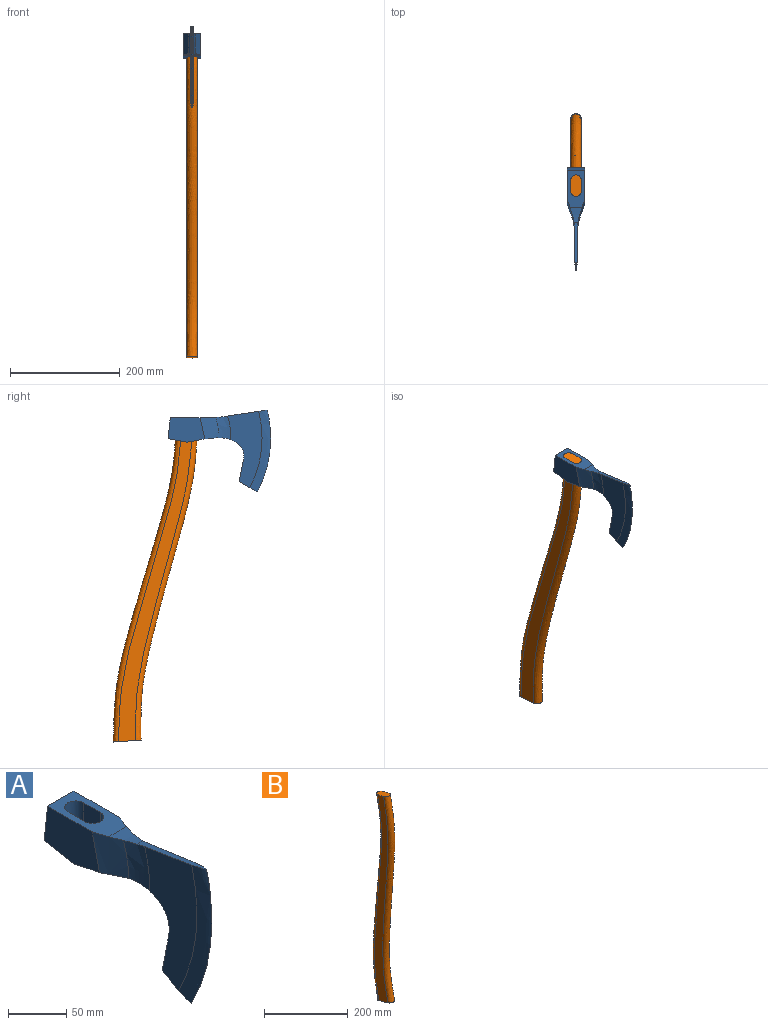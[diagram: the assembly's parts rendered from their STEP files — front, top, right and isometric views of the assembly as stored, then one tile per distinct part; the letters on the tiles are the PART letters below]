
ASSEMBLY  parts=2 mates=1
PART A: 27 faces, bbox 32.4x187.8x151 mm
  f0: plane 69.14x31.75mm, normal (0,0,1), area 1447.6mm2, adj f14,f16,f17,f18,f19,f20,f21,f22
  f1: plane 31.75x23.41mm, normal (0,-0.2,-0.98), area 477.4mm2, adj f2,f17,f18,f20,f22,f23,f26
  f2: bspline ~35.85x31.75mm, area 757.3mm2, adj f1,f17,f18,f19,f20,f21,f22
  f3: revolved ~44.09x28.22mm, area 891.3mm2, adj f4,f9,f13,f16,f24,f25
  f4: revolved ~141.11x70.47mm, area 5346.3mm2, adj f3,f5,f9,f11,f12,f13
  f5: revolved ~150.44x38.1mm, area 2375.4mm2, adj f4,f9,f10,f11
  f6: revolved ~150.44x38.1mm, area 2375.4mm2, adj f7,f9,f10,f11
  f7: revolved ~141.11x70.47mm, area 5346.3mm2, adj f6,f8,f9,f11,f12,f13
  f8: revolved ~44.09x28.22mm, area 891.3mm2, adj f7,f9,f13,f14,f24,f25
  f9: plane 81.06x12.42mm, normal (0,0.15,0.99), area 394.5mm2, adj f3,f4,f5,f6,f7,f8,f24
  f10: cylinder r=209.66mm len=149.23mm, axis (-1,0,0), area 5.1mm2, adj f5,f6,f11
  f11: plane 33.95x19.05mm, normal (0,0.48,-0.88), area 156.1mm2, adj f4,f5,f6,f7,f10,f12
  f12: plane 40.5x7.94mm, normal (0,0.98,0.19), area 208.4mm2, adj f4,f7,f11,f13
  f13: extruded ~38.79x35.05mm, area 328.8mm2, adj f3,f4,f7,f8,f12,f25
  f14: bspline ~38.88x34.67mm, area 1113.1mm2, adj f0,f8,f15,f17,f24,f25,f26
  f15: plane 25.97x12.75mm, normal (0,-0.08,-1), area 271.9mm2, adj f14,f16,f25,f26
  f16: bspline ~38.88x34.67mm, area 1113.1mm2, adj f0,f3,f15,f18,f24,f25,f26
  f17: plane 67.01x44.45mm, normal (1,0,0), area 2520mm2, adj f0,f1,f2,f14,f19,f26
  f18: plane 67.01x44.45mm, normal (-1,0,0), area 2520mm2, adj f0,f1,f2,f16,f19,f26
  f19: plane 38.1x31.75mm, normal (0,0.99,0.11), area 1216.7mm2, adj f0,f2,f17,f18
  f20: plane 44.58x20.45mm, normal (-1,0,0), area 870.5mm2, adj f0,f1,f2,f21,f23
  f21: cylinder r=9.53mm len=40.76mm, axis (0,0,1), area 1174.2mm2, adj f0,f2,f20,f22
  f22: plane 44.58x20.45mm, normal (1,0,0), area 870.5mm2, adj f0,f1,f2,f21,f23
  f23: cylinder r=9.53mm len=43.02mm, axis (0,0,1), area 1250.4mm2, adj f0,f1,f20,f22
  f24: cylinder r=177.8mm len=26.67mm, axis (-1,0,0), area 361.9mm2, adj f0,f3,f8,f9,f14,f16
  f25: cylinder r=63.5mm len=16.55mm, axis (-1,0,0), area 183.8mm2, adj f3,f8,f13,f14,f15,f16
  f26: cylinder r=127mm len=31.75mm, axis (1,0,0), area 475.6mm2, adj f1,f14,f15,f16,f17,f18
PART B: 6 faces, bbox 20.2x68.7x610.7 mm
  f0: plane 49.76x19.75mm, normal (0,-0.26,-0.97), area 889.9mm2, adj f2,f3,f4,f5
  f1: plane 38.95x19.38mm, normal (0,0.19,0.98), area 672.1mm2, adj f2,f3,f4,f5
  f2: bspline ~603.8x39.22mm, area 18094.7mm2, adj f0,f1,f3,f5
  f3: plane 606.38x46.73mm, normal (-1,0,0), area 14745.1mm2, adj f0,f1,f2,f4
  f4: bspline ~598.89x27.47mm, area 17941.8mm2, adj f0,f1,f3,f5
  f5: plane 606.38x46.73mm, normal (1,0,0), area 14729.1mm2, adj f0,f1,f2,f4
PLACE A rot(axis=(0,0,-1),0deg) t=(-21.93,-13.45,3.53)mm
PLACE B rot(axis=(1,0,0),11.2deg) t=(-21.93,74.22,-552.83)mm
MATE parallel B.f1 <-> A.f0  axis (0,0,1) through (-31.45,-10.28,47.98)mm
